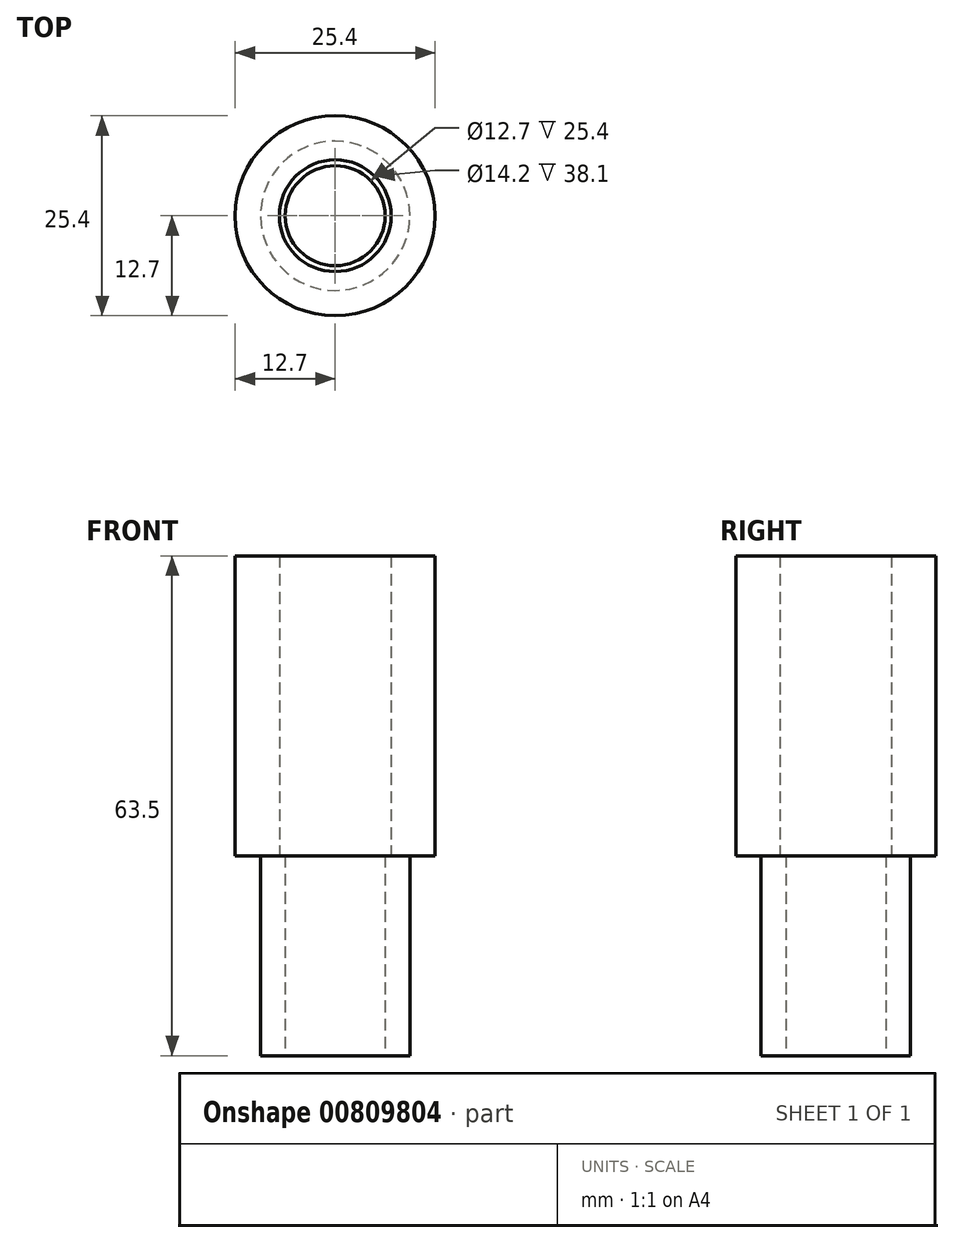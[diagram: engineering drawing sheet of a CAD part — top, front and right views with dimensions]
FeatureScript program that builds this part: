
annotation { "Feature Type Name" : "Feature", "Feature Type Description" : "" }
export const myFeature = defineFeature(function(context is Context, id is Id, definition is map)
    precondition{}
    {
        {
            var Q0;
            Q0=qCreatedBy(makeId("Top.planeOp"),FACE);
            var sketch = newSketch(context, id + "F0", { "sketchPlane" : qUnion([Q0])});
            skCircle(sketch, "E0", {"center": v(0, 0) * mm, "radius": 6.35 * mm});
            skCircle(sketch, "E1", {"center": v(0, 0) * mm, "radius": 9.48 * mm});
            skSolve(sketch);
        }
        {
            var Q0;
            Q0=qSketchRegion(id+"F0",true);
            extrude(context, id + "F1", {"entities" : qUnion([Q0]), "depth" : 25.4 * mm, "offsetDistance" : 25.4 * mm});
        }
        {
            var Q0;
            Q0=makeQuery(id+"F1.opExtrude","CAP_FACE",FACE,{"disambiguationData":[OSD([sQuery(id+"F0.wireOp",EDGE,"E0"),sQuery(id+"F0.wireOp",EDGE,"E1")])],"isStart":false});
            var sketch = newSketch(context, id + "F2", { "sketchPlane" : qUnion([Q0])});
            skCircle(sketch, "E2", {"center": v(0, 0) * mm, "radius": 7.1 * mm});
            skCircle(sketch, "E3", {"center": v(0, 0) * mm, "radius": 12.7 * mm});
            skSolve(sketch);
        }
        {
            var Q0;
            Q0=qSketchRegion(id+"F2",true);
            extrude(context, id + "F3", {"entities" : qUnion([Q0]), "operationType" : NewBodyOperationType.ADD, "depth" : 38.1 * mm, "offsetDistance" : 25.4 * mm});
        }
    });
